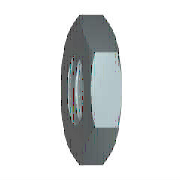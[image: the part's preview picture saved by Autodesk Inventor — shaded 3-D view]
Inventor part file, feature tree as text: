
AUTODESK INVENTOR PART (.ipt)
format: ipt  version: 2022 (Build 260153000, 153)  size: 176,640 bytes
history: native  units: mm (DEFAULTED — no unit token found)
features: sketch x3, other x2, extrude x1, hole x1, plane x1
ambient origin geometry x7: Origin, YZ Plane, XZ Plane, X Axis, Y Axis, Z Axis, Center Point
bodies: Solid1 (feature_tree)
feature tree (8):
  extrude  "Базовый элемент"  Depth=8.082904mm
  other  "Фаска1"
  hole  "Резьба"  [1 undecoded]
  other  "Work Axis1"
  plane  "Work Plane1"
  sketch  "Эскиз1"
  sketch  "Эскиз2"
  sketch  "Эскиз3"
note: 1 required parameter value undecoded (feature->parameter linkage not recoverable at this tier; creation-order binding heuristic only, values carry confidence <= 0.55)
